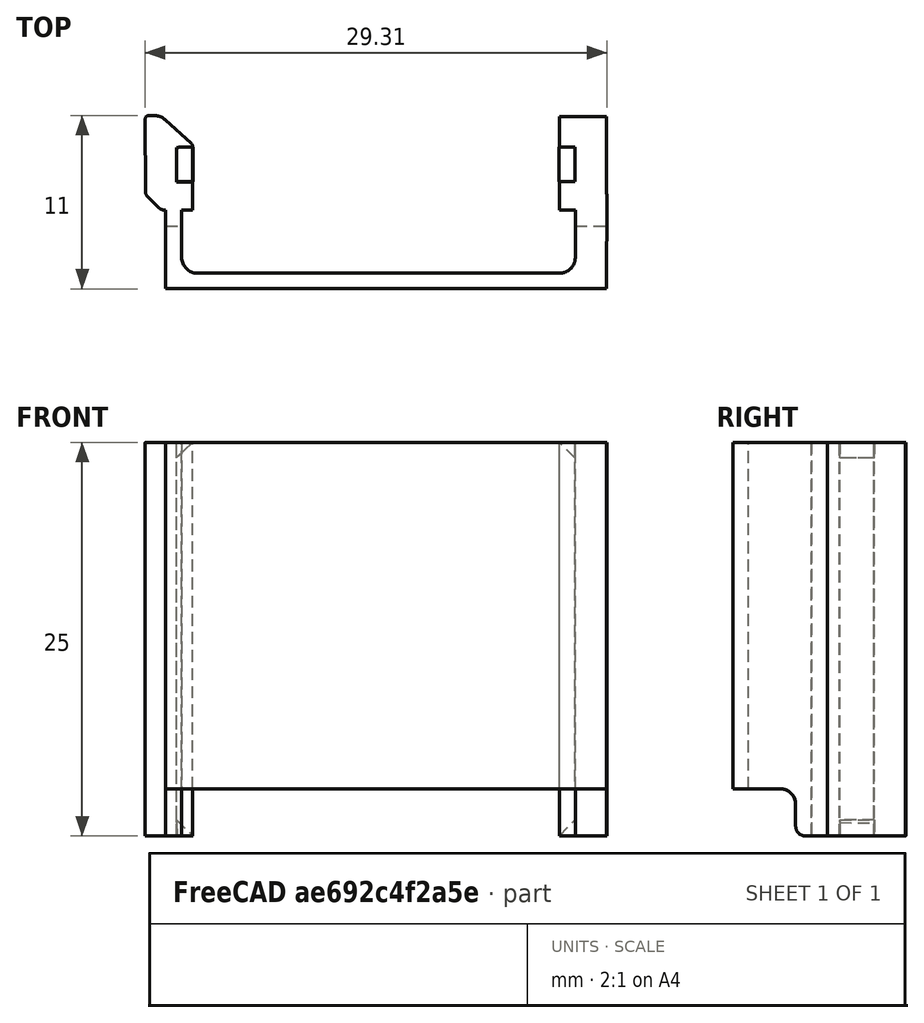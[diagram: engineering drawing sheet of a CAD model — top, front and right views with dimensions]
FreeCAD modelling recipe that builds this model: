
FCSTD DOCUMENT  (FreeCAD 0.18.4R)
Label: GSMBoardClip
License: All rights reserved
LicenseURL: http://en.wikipedia.org/wiki/All_rights_reserved
objects: Sketcher::SketchObject×7, PartDesign::Pad×7, Part::Fillet×4, Part::MultiFuse×1, Part::Box×1, Part::Cut×1, Mesh::Feature×1
note: 28 computed .brp shape members not serialized (recipe doc carries the construction recipe); baked Part::Feature solids carry a one-line shape summary decoded from their .brp

FEATURE [Sketcher::SketchObject] Sketch
  MapMode = 5
  sketch-geometry (8):
    g0: LineSegment StartX=-13.9838 StartY=-7.01134 StartZ=0 EndX=11.0144 EndY=-7.01134 EndZ=0
    g1: LineSegment StartX=13.0015 StartY=-7.99791 StartZ=0 EndX=-14.9987 EndY=-7.99791 EndZ=0
    g2: LineSegment StartX=-14.9987 StartY=-1.98555 StartZ=0 EndX=-13.9838 EndY=-1.98555 EndZ=0
    g3: LineSegment StartX=-13.9838 StartY=-1.98555 StartZ=0 EndX=-13.9838 EndY=-7.01134 EndZ=0
    g4: LineSegment StartX=-14.9987 StartY=-7.99791 StartZ=0 EndX=-14.9987 EndY=-1.98555 EndZ=0
    g5: LineSegment StartX=11.0144 StartY=-7.01134 StartZ=0 EndX=11.0098 EndY=-1.99154 EndZ=0
    g6: LineSegment StartX=11.0098 StartY=-1.99154 StartZ=0 EndX=13.0105 EndY=-1.99613 EndZ=0
    g7: LineSegment StartX=13.0105 StartY=-1.99613 StartZ=0 EndX=13.0015 EndY=-7.99791 EndZ=0
  constraints (13):
    c: Horizontal(g0)
    c: Horizontal(g1)
    c: Coincident(g2,g3)
    c: Coincident(g4,g2)
    c: Horizontal(g2)
    c: Vertical(g3)
    c: Vertical(g4)
    c: Coincident(g0,g3)
    c: Coincident(g4,g1)
    c: Coincident(g1,g7)
    c: Coincident(g0,g5)
    c: Coincident(g5,g6)
    c: Coincident(g6,g7)
FEATURE [PartDesign::Pad] Pad
  Length = 25
  Length2 = 100
  Profile = -> Sketch
  Type = 0
FEATURE [Sketcher::SketchObject] Sketch001
  MapMode = 5
  Placement = pos=(-5.3,1,0) rot=(0,0,1;0rad)
  sketch-geometry (16):
    g0: LineSegment StartX=-9.71523 StartY=1.72867 StartZ=0 EndX=-8.08435 EndY=0.245826 EndZ=0
    g1: LineSegment StartX=-7.98874 StartY=0.0408415 StartZ=0 EndX=-7.98646 EndY=-0.016209 EndZ=0
    g2: LineSegment StartX=-7.98646 StartY=-0.016209 StartZ=0 EndX=-8.99915 EndY=-0.016209 EndZ=0
    g3: LineSegment StartX=-8.99915 StartY=-0.016209 StartZ=0 EndX=-8.99963 EndY=-2.20954 EndZ=0
    g4: LineSegment StartX=-8.99963 StartY=-2.20954 StartZ=0 EndX=-7.98693 EndY=-2.20954 EndZ=0
    g5: LineSegment StartX=-7.98693 StartY=-2.20954 StartZ=0 EndX=-7.98975 EndY=-3.99998 EndZ=0
    g6: LineSegment StartX=-7.98975 StartY=-3.99998 StartZ=0 EndX=-8.9894 EndY=-3.99998 EndZ=0
    g7: LineSegment StartX=-8.9894 StartY=-3.99998 StartZ=0 EndX=-9.78688 EndY=-3.99531 EndZ=0
    g8: LineSegment StartX=-10.1428 StartY=-3.84773 StartZ=0 EndX=-10.8579 EndY=-3.14001 EndZ=0
    g9: LineSegment StartX=-10.9954 StartY=-2.81068 StartZ=0 EndX=-10.9987 EndY=1.79469 EndZ=0
    g10: LineSegment StartX=-10.7942 StartY=1.99973 StartZ=0 EndX=-10.4199 EndY=2.0004 EndZ=0
    g11: ArcOfCircle CenterX=-10.7939 CenterY=1.79484 CenterZ=0 NormalX=0 NormalY=0 NormalZ=1 AngleXU=0 Radius=0.204891 StartAngle=1.57259 EndAngle=3.14232
    g12: ArcOfCircle CenterX=-10.418 CenterY=0.955743 CenterZ=0 NormalX=0 NormalY=0 NormalZ=1 AngleXU=0 Radius=1.04466 StartAngle=0.832904 EndAngle=1.57259
    g13: ArcOfCircle CenterX=-8.28137 CenterY=0.0291366 CenterZ=0 NormalX=0 NormalY=0 NormalZ=1 AngleXU=0 Radius=0.292868 StartAngle=0.0399774 EndAngle=0.832904
    g14: ArcOfCircle CenterX=-10.5316 CenterY=-2.81035 CenterZ=0 NormalX=0 NormalY=0 NormalZ=1 AngleXU=0 Radius=0.463836 StartAngle=3.14232 EndAngle=3.93213
    g15: ArcOfCircle CenterX=-9.78389 CenterY=-3.4851 CenterZ=0 NormalX=0 NormalY=0 NormalZ=1 AngleXU=0 Radius=0.510226 StartAngle=3.93213 EndAngle=4.70654
  constraints (16):
    c: Coincident(g1,g2)
    c: Coincident(g2,g3)
    c: Coincident(g3,g4)
    c: Coincident(g4,g5)
    c: Coincident(g5,g6)
    c: Coincident(g6,g7)
    c: Tangent(g10,g11) = 1.5708
    c: Tangent(g9,g11) = 1.5708
    c: Tangent(g10,g12) = 1.5708
    c: Tangent(g0,g12) = 1.5708
    c: Tangent(g0,g13) = 1.5708
    c: Tangent(g1,g13) = 1.5708
    c: Tangent(g9,g14) = 1.5708
    c: Tangent(g8,g14) = 1.5708
    c: Tangent(g8,g15) = 1.5708
    c: Tangent(g7,g15) = 1.5708
FEATURE [PartDesign::Pad] Pad001  label="Snap"
  Length = 25
  Length2 = 100
  Placement = pos=(-5.3,1,0) rot=(0,0,1;0rad)
  Profile = -> Sketch001
  Type = 0
FEATURE [Sketcher::SketchObject] Sketch002
  MapMode = 5
  Placement = pos=(12,-2,0) rot=(0,0,1;0rad)
  sketch-geometry (8):
    g0: LineSegment StartX=-2.00228 StartY=4.95368 StartZ=0 EndX=1.00739 EndY=4.95368 EndZ=0
    g1: LineSegment StartX=1.00739 StartY=4.95368 StartZ=0 EndX=1.00739 EndY=-1.00779 EndZ=0
    g2: LineSegment StartX=1.00739 StartY=-1.00779 StartZ=0 EndX=-2.00228 EndY=-1.00779 EndZ=0
    g3: LineSegment StartX=-2.00228 StartY=-1.00779 StartZ=0 EndX=-2.00228 EndY=0.799757 EndZ=0
    g4: LineSegment StartX=-2.00228 StartY=3.00495 StartZ=0 EndX=-0.994359 EndY=3.0082 EndZ=0
    g5: LineSegment StartX=-2.00228 StartY=0.799757 StartZ=0 EndX=-0.998568 EndY=0.798759 EndZ=0
    g6: LineSegment StartX=-0.994359 StartY=3.0082 StartZ=0 EndX=-0.998568 EndY=0.798759 EndZ=0
    g7: LineSegment StartX=-2.00228 StartY=3.00495 StartZ=0 EndX=-2.00228 EndY=4.95368 EndZ=0
  constraints (13):
    c: Coincident(g0,g1)
    c: Coincident(g1,g2)
    c: Coincident(g2,g3)
    c: Coincident(g7,g0)
    c: Horizontal(g0)
    c: Horizontal(g2)
    c: Vertical(g1)
    c: Vertical(g3)
    c: Tangent(g3,g7)
    c: Coincident(g4,g7)
    c: Coincident(g4,g6)
    c: Coincident(g6,g5)
    c: Coincident(g5,g3)
FEATURE [PartDesign::Pad] Pad002  label="Solid"
  Length = 25
  Length2 = 100
  Placement = pos=(12,-2,0) rot=(0,0,1;0rad)
  Profile = -> Sketch002
  Type = 0
FEATURE [Sketcher::SketchObject] Sketch004
  MapMode = 5
  Placement = pos=(-7.3,1,6.03) rot=(1,0,0;1.5708rad)
  sketch-geometry (3):
    g0: LineSegment StartX=-7.00166 StartY=-5.01077 StartZ=0 EndX=-6.98953 EndY=-6.02972 EndZ=0
    g1: LineSegment StartX=-6.98953 StartY=-6.02972 StartZ=0 EndX=-5.96627 EndY=-6.02972 EndZ=0
    g2: LineSegment StartX=-7.00166 StartY=-5.01077 StartZ=0 EndX=-5.96627 EndY=-6.02972 EndZ=0
  constraints (3):
    c: Coincident(g0,g1)
    c: Coincident(g2,g0)
    c: Coincident(g2,g1)
FEATURE [PartDesign::Pad] Pad004  label="stopper002"
  Length = 2.2
  Length2 = 100
  Placement = pos=(-7.3,1,6.03) rot=(1,0,0;1.5708rad)
  Profile = -> Sketch004
  Type = 0
FEATURE [Sketcher::SketchObject] Sketch006
  MapMode = 5
  Placement = pos=(11,1,0.03) rot=(1,0,0;1.5708rad)
  sketch-geometry (3):
    g0: LineSegment StartX=-0.005347 StartY=0.971544 StartZ=0 EndX=-0.005347 EndY=-0.027131 EndZ=0
    g1: LineSegment StartX=-0.005347 StartY=-0.027131 StartZ=0 EndX=-1.00402 EndY=-0.027124 EndZ=0
    g2: LineSegment StartX=-1.00402 StartY=-0.027124 StartZ=0 EndX=-0.005347 EndY=0.971544 EndZ=0
  constraints (3):
    c: Coincident(g0,g1)
    c: Coincident(g1,g2)
    c: Coincident(g2,g0)
FEATURE [PartDesign::Pad] Pad006  label="stopper003"
  Length = 2.2
  Length2 = 100
  Placement = pos=(11,1,0.03) rot=(1,0,0;1.5708rad)
  Profile = -> Sketch006
  Type = 0
FEATURE [Sketcher::SketchObject] Sketch007
  MapMode = 5
  Placement = pos=(11,1,24.03) rot=(1,0,0;1.5708rad)
  sketch-geometry (3):
    g0: LineSegment StartX=-0.005347 StartY=0.971544 StartZ=0 EndX=-0.005347 EndY=-0.027131 EndZ=0
    g1: LineSegment StartX=-0.005347 StartY=-0.027131 StartZ=0 EndX=-1.00779 EndY=0.969763 EndZ=0
    g2: LineSegment StartX=-1.00779 StartY=0.969763 StartZ=0 EndX=-0.005347 EndY=0.971544 EndZ=0
  constraints (3):
    c: Coincident(g0,g1)
    c: Coincident(g1,g2)
    c: Coincident(g2,g0)
FEATURE [PartDesign::Pad] Pad007  label="stopper004"
  Length = 2.2
  Length2 = 100
  Placement = pos=(11,1,24.03) rot=(1,0,0;1.5708rad)
  Profile = -> Sketch007
  Type = 0
FEATURE [Sketcher::SketchObject] Sketch008
  MapMode = 5
  Placement = pos=(-13.3,1,24.03) rot=(1,0,0;1.5708rad)
  sketch-geometry (3):
    g0: LineSegment StartX=-0.005347 StartY=0.971544 StartZ=0 EndX=-1.00207 EndY=-0.002707 EndZ=0
    g1: LineSegment StartX=-1.00207 StartY=-0.002707 StartZ=0 EndX=-1.00779 EndY=0.969763 EndZ=0
    g2: LineSegment StartX=-1.00779 StartY=0.969763 StartZ=0 EndX=-0.005347 EndY=0.971544 EndZ=0
  constraints (3):
    c: Coincident(g0,g1)
    c: Coincident(g1,g2)
    c: Coincident(g2,g0)
FEATURE [PartDesign::Pad] Pad008  label="stopper001"
  Length = 2.2
  Length2 = 100
  Placement = pos=(-13.3,1,24.03) rot=(1,0,0;1.5708rad)
  Profile = -> Sketch008
  Type = 0
FEATURE [Part::MultiFuse] Fusion
  Shapes = -> [Pad,Pad007,Pad006,Pad002,Pad004,Pad001,Pad008]
FEATURE [Part::Box] Box  label="Würfel"
  AttacherType = Attacher::AttachEngine3D
  Height = 5
  Length = 31
  Placement = pos=(-17,-9,-2) rot=(0,0,1;0rad)
  Width = 5
FEATURE [Part::Fillet] Fillet
  Base = -> Box
  Edges = 1 edges r=1: [Edge12]
FEATURE [Part::Cut] Cut
  Base = -> Fusion
  Tool = -> Fillet
FEATURE [Part::Fillet] Fillet001
  Base = -> Cut
  Edges = 1 edges r=0.6: [Edge42]
FEATURE [Part::Fillet] Fillet002
  Base = -> Fillet001
  Edges = 1 edges r=0.6: [Edge82]
FEATURE [Part::Fillet] Fillet003
  Base = -> Fillet002
  Edges = 2 edges r=1: [Edge7,Edge33]
FEATURE [Mesh::Feature] Mesh  label="Fillet003 (Meshed)"
